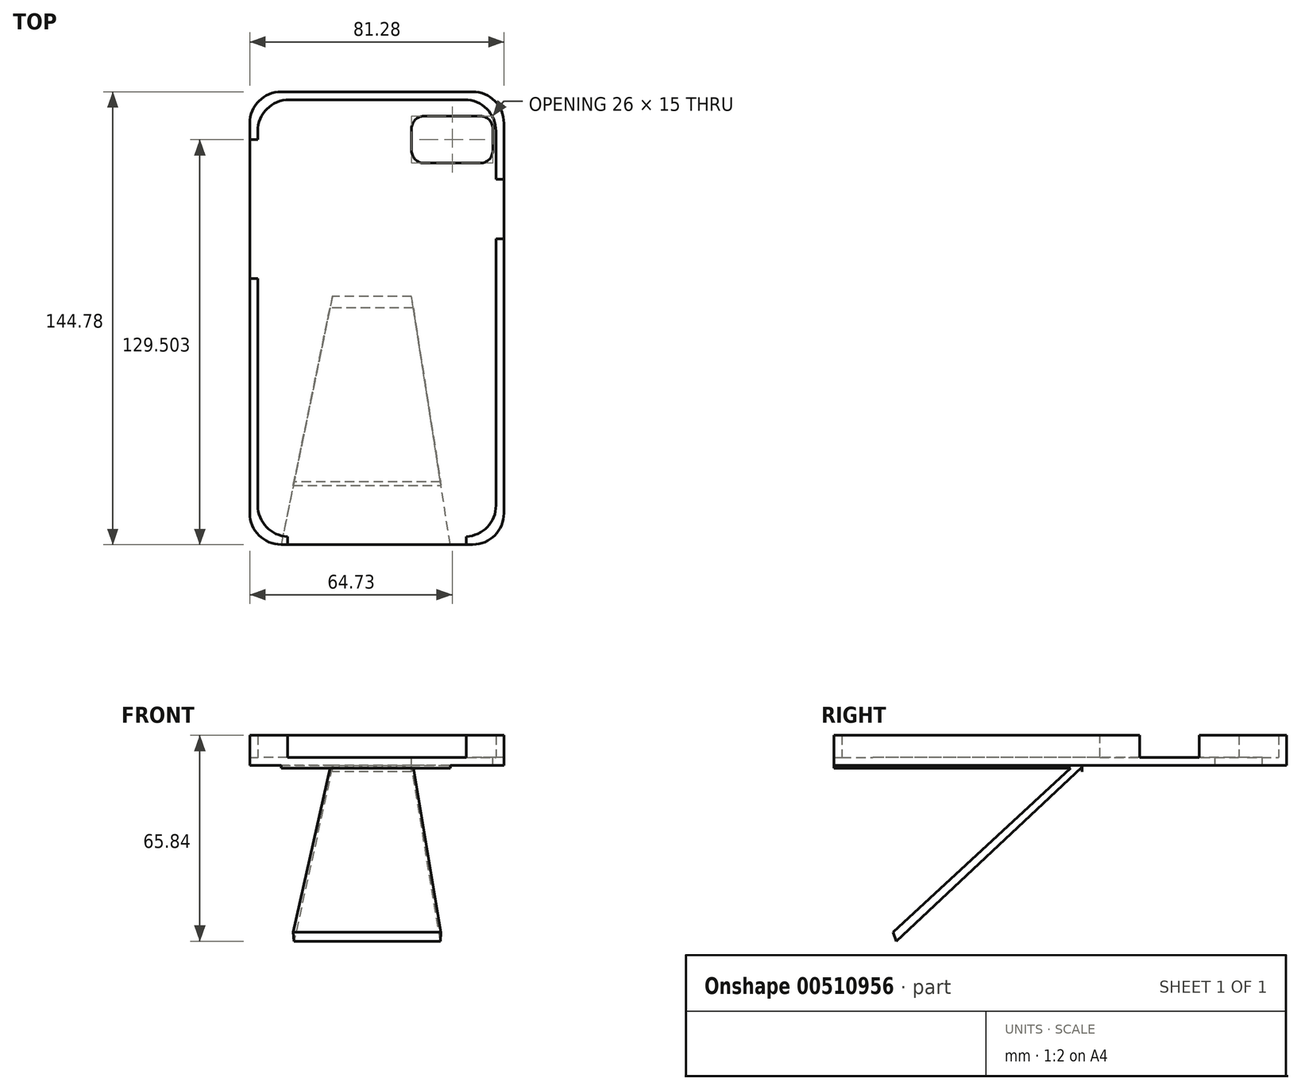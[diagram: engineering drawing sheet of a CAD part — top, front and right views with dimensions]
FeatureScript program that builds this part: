
annotation { "Feature Type Name" : "Feature", "Feature Type Description" : "" }
export const myFeature = defineFeature(function(context is Context, id is Id, definition is map)
    precondition{}
    {
        {
            var Q0;
            Q0=qCreatedBy(makeId("Top.planeOp"),FACE);
            var sketch = newSketch(context, id + "F0", { "sketchPlane" : qUnion([Q0])});
            skLineSegment(sketch, "E0.bottom", {"start": v(-49.2, 70.21) * mm, "end": v(27, 70.21) * mm});
            skLineSegment(sketch, "E0.top", {"start": v(-49.2, -69.49) * mm, "end": v(27, -69.49) * mm});
            skLineSegment(sketch, "E0.left", {"start": v(-49.2, 70.21) * mm, "end": v(-49.2, -69.49) * mm});
            skLineSegment(sketch, "E0.right", {"start": v(27, 70.21) * mm, "end": v(27, -69.49) * mm});
            skSolve(sketch);
        }
        {
            var Q0;
            Q0=makeQuery(id+"F0.imprint","IMPRINT",FACE,{"disambiguationData":[TD([[makeQuery(id+"F0.imprint","IMPRINT",EDGE,{"derivedFrom":sQuery(id+"F0.wireOp",EDGE,"E0.bottom")}),-1.0]])]});
            extrude(context, id + "F1", {"entities" : qUnion([Q0]), "depth" : 7.1 * mm, "offsetDistance" : 25 * mm});
        }
        {
            var Q0;
            Q0=makeQuery(id+"F1.opExtrude","CAP_FACE",FACE,{"disambiguationData":[OSD([sQuery(id+"F0.wireOp",EDGE,"E0.bottom"),sQuery(id+"F0.wireOp",EDGE,"E0.top"),sQuery(id+"F0.wireOp",EDGE,"E0.left"),sQuery(id+"F0.wireOp",EDGE,"E0.right")])],"isStart":false});
            shell(context, id + "F2", {"entities" : qUnion([Q0]), "thickness" : 2.54 * mm, "oppositeDirection" : true});
        }
        {
            var Q0;
            Q0=makeQuery(id+"F2.opShell","OFFSET_FACE",FACE,{"disambiguationData":[OSD([sQuery(id+"F0.wireOp",EDGE,"E0.left")])]});
            var sketch = newSketch(context, id + "F3", { "sketchPlane" : qUnion([Q0])});
            skLineSegment(sketch, "E1.bottom", {"start": v(57.51, 7.1) * mm, "end": v(13.06, 7.1) * mm});
            skLineSegment(sketch, "E1.top", {"start": v(57.51, 0) * mm, "end": v(13.06, 0) * mm});
            skLineSegment(sketch, "E1.left", {"start": v(57.51, 7.1) * mm, "end": v(57.51, 0) * mm});
            skLineSegment(sketch, "E1.right", {"start": v(13.06, 7.1) * mm, "end": v(13.06, 0) * mm});
            skSolve(sketch);
        }
        {
            var Q0;
            Q0=makeQuery(id+"F3.imprint","IMPRINT",FACE,{"disambiguationData":[TD([[makeQuery(id+"F3.imprint","IMPRINT",EDGE,{"derivedFrom":sQuery(id+"F3.wireOp",EDGE,"E1.bottom")}),1.0]])]});
            var Q1;
            Q1=makeQuery(id+"F1.opExtrude","SWEPT_FACE",FACE,{"disambiguationData":[OSD([sQuery(id+"F0.wireOp",EDGE,"E0.left")])]});
            extrude(context, id + "F4", {"entities" : qUnion([Q0, Q1]), "operationType" : NewBodyOperationType.REMOVE, "oppositeDirection" : true, "depth" : 25.4 * mm});
        }
        {
            var Q0;
            Q0=makeQuery(id+"F2.opShell","OFFSET_FACE",FACE,{"disambiguationData":[OSD([sQuery(id+"F0.wireOp",EDGE,"E0.right")])]});
            var sketch = newSketch(context, id + "F5", { "sketchPlane" : qUnion([Q0])});
            skLineSegment(sketch, "E2.bottom", {"start": v(-44.81, 7.1) * mm, "end": v(-25.76, 7.1) * mm});
            skLineSegment(sketch, "E2.top", {"start": v(-44.81, 0) * mm, "end": v(-25.76, 0) * mm});
            skLineSegment(sketch, "E2.left", {"start": v(-44.81, 7.1) * mm, "end": v(-44.81, 0) * mm});
            skLineSegment(sketch, "E2.right", {"start": v(-25.76, 7.1) * mm, "end": v(-25.76, 0) * mm});
            skSolve(sketch);
        }
        {
            var Q0;
            Q0=makeQuery(id+"F5.imprint","IMPRINT",FACE,{"disambiguationData":[TD([[makeQuery(id+"F5.imprint","IMPRINT",EDGE,{"derivedFrom":sQuery(id+"F5.wireOp",EDGE,"E2.bottom")}),-1.0]])]});
            extrude(context, id + "F6", {"entities" : qUnion([Q0]), "operationType" : NewBodyOperationType.REMOVE, "oppositeDirection" : true, "depth" : 25.4 * mm});
        }
        {
            var Q0;
            Q0=makeQuery(id+"F2.opShell","OFFSET_FACE",FACE,{"disambiguationData":[OSD([sQuery(id+"F0.wireOp",EDGE,"E0.top")])]});
            var sketch = newSketch(context, id + "F7", { "sketchPlane" : qUnion([Q0])});
            skLineSegment(sketch, "E3.bottom", {"start": v(-17.48, 7.1) * mm, "end": v(39.67, 7.1) * mm});
            skLineSegment(sketch, "E3.top", {"start": v(-17.48, 0) * mm, "end": v(39.67, 0) * mm});
            skLineSegment(sketch, "E3.left", {"start": v(-17.48, 7.1) * mm, "end": v(-17.48, 0) * mm});
            skLineSegment(sketch, "E3.right", {"start": v(39.67, 7.1) * mm, "end": v(39.67, 0) * mm});
            skSolve(sketch);
        }
        {
            var Q0;
            Q0 = qSketchRegion(id + "F7", true);
            extrude(context, id + "F8", {"entities" : qUnion([Q0]), "operationType" : NewBodyOperationType.REMOVE, "oppositeDirection" : true, "depth" : 25.4 * mm});
        }
        {
            var Q0;
            Q0=makeQuery(id+"F2.opShell","OFFSET_EDGE",EDGE,{"disambiguationData":[OSD([sQuery(id+"F0.wireOp",EDGE,"E0.bottom"),sQuery(id+"F0.wireOp",EDGE,"E0.right")])]});
            var Q1;
            Q1=makeQuery(id+"F2.opShell","OFFSET_EDGE",EDGE,{"disambiguationData":[OSD([sQuery(id+"F0.wireOp",EDGE,"E0.bottom"),sQuery(id+"F0.wireOp",EDGE,"E0.left")])]});
            var Q2;
            Q2=makeQuery(id+"F2.opShell","OFFSET_EDGE",EDGE,{"disambiguationData":[OSD([sQuery(id+"F0.wireOp",EDGE,"E0.top"),sQuery(id+"F0.wireOp",EDGE,"E0.left")])]});
            var Q3;
            Q3=makeQuery(id+"F2.opShell","OFFSET_EDGE",EDGE,{"disambiguationData":[OSD([sQuery(id+"F0.wireOp",EDGE,"E0.top"),sQuery(id+"F0.wireOp",EDGE,"E0.right")])]});
            fillet(context, id + "F9", {"entities" : qUnion([Q0, Q1, Q2, Q3]), "radius" : 10 * mm, "tangentPropagation" : true, "allowEdgeOverflow" : false});
        }
        {
            var Q0;
            Q0=makeQuery(id+"F1.opExtrude","SWEPT_EDGE",EDGE,{"disambiguationData":[OSD([sQuery(id+"F0.wireOp",EDGE,"E0.top"),sQuery(id+"F0.wireOp",EDGE,"E0.right")])]});
            var Q1;
            Q1=makeQuery(id+"F1.opExtrude","SWEPT_EDGE",EDGE,{"disambiguationData":[OSD([sQuery(id+"F0.wireOp",EDGE,"E0.top"),sQuery(id+"F0.wireOp",EDGE,"E0.left")])]});
            var Q2;
            Q2=makeQuery(id+"F1.opExtrude","SWEPT_EDGE",EDGE,{"disambiguationData":[OSD([sQuery(id+"F0.wireOp",EDGE,"E0.bottom"),sQuery(id+"F0.wireOp",EDGE,"E0.right")])]});
            var Q3;
            Q3=makeQuery(id+"F1.opExtrude","SWEPT_EDGE",EDGE,{"disambiguationData":[OSD([sQuery(id+"F0.wireOp",EDGE,"E0.bottom"),sQuery(id+"F0.wireOp",EDGE,"E0.left")])]});
            fillet(context, id + "F10", {"entities" : qUnion([Q0, Q1, Q2, Q3]), "radius" : 10 * mm, "tangentPropagation" : true, "allowEdgeOverflow" : false});
        }
        {
            var Q0;
            Q0=makeQuery(id+"F8.boolean.opBoolean","MERGE",FACE,{"derivedFrom":[makeQuery(id+"F6.boolean.opBoolean","MERGE",FACE,{"derivedFrom":[makeQuery(id+"F4.boolean.opBoolean","MERGE",FACE,{"derivedFrom":[makeQuery(id+"F2.opShell","OFFSET_FACE",FACE,{"disambiguationData":[OSD([sQuery(id+"F0.wireOp",EDGE,"E0.bottom"),sQuery(id+"F0.wireOp",EDGE,"E0.top"),sQuery(id+"F0.wireOp",EDGE,"E0.left"),sQuery(id+"F0.wireOp",EDGE,"E0.right")])]}),makeQuery(id+"F4.opExtrude","SWEPT_FACE",FACE,{"disambiguationData":[OSD([sQuery(id+"F3.wireOp",EDGE,"E1.top")])]})]}),makeQuery(id+"F6.opExtrude","SWEPT_FACE",FACE,{"disambiguationData":[OSD([sQuery(id+"F5.wireOp",EDGE,"E2.top")])]})]}),makeQuery(id+"F8.opExtrude","SWEPT_FACE",FACE,{"disambiguationData":[OSD([sQuery(id+"F7.wireOp",EDGE,"E3.top")])]})]});
            var sketch = newSketch(context, id + "F11", { "sketchPlane" : qUnion([Q0])});
            skLineSegment(sketch, "E4.bottom", {"start": v(4, 64.97) * mm, "end": v(22, 64.97) * mm});
            skLineSegment(sketch, "E4.top", {"start": v(4, 49.97) * mm, "end": v(22, 49.97) * mm});
            skLineSegment(sketch, "E4.left", {"start": v(0, 60.97) * mm, "end": v(0, 53.97) * mm});
            skLineSegment(sketch, "E4.right", {"start": v(26, 60.97) * mm, "end": v(26, 53.97) * mm});
            skPoint(sketch, "E5.visualSharp", {"position": v(0, 49.97) * mm});
            skArc(sketch, "E5.filletArc", {"start": v(0, 53.97) * mm, "mid": v(1.17, 51.14) * mm, "end": v(4, 49.97) * mm});
            skPoint(sketch, "E6.visualSharp", {"position": v(0, 64.97) * mm});
            skArc(sketch, "E6.filletArc", {"start": v(4, 64.97) * mm, "mid": v(1.17, 63.8) * mm, "end": v(0, 60.97) * mm});
            skPoint(sketch, "E7.visualSharp", {"position": v(26, 64.97) * mm});
            skArc(sketch, "E7.filletArc", {"start": v(26, 60.97) * mm, "mid": v(24.83, 63.8) * mm, "end": v(22, 64.97) * mm});
            skPoint(sketch, "E8.visualSharp", {"position": v(26, 49.97) * mm});
            skArc(sketch, "E8.filletArc", {"start": v(22, 49.97) * mm, "mid": v(24.83, 51.14) * mm, "end": v(26, 53.97) * mm});
            skSolve(sketch);
        }
        {
            var Q0;
            Q0=makeQuery(id+"F11.imprint","IMPRINT",FACE,{"disambiguationData":[TD([[makeQuery(id+"F11.imprint","IMPRINT",EDGE,{"derivedFrom":sQuery(id+"F11.wireOp",EDGE,"E4.bottom")}),-1.0]])]});
            extrude(context, id + "F12", {"entities" : qUnion([Q0]), "operationType" : NewBodyOperationType.REMOVE, "oppositeDirection" : true, "depth" : 25 * mm, "offsetDistance" : 25 * mm});
        }
        {
            var Q0;
            Q0=makeQuery(id+"F1.opExtrude","CAP_FACE",FACE,{"disambiguationData":[OSD([sQuery(id+"F0.wireOp",EDGE,"E0.bottom"),sQuery(id+"F0.wireOp",EDGE,"E0.top"),sQuery(id+"F0.wireOp",EDGE,"E0.left"),sQuery(id+"F0.wireOp",EDGE,"E0.right")])],"isStart":true});
            var sketch = newSketch(context, id + "F13", { "sketchPlane" : qUnion([Q0])});
            skLineSegment(sketch, "E9", {"start": v(0, -7.34) * mm, "end": v(-25.34, -7.34) * mm});
            skLineSegment(sketch, "E10", {"start": v(-25.34, -7.34) * mm, "end": v(-41.73, 72.03) * mm});
            skLineSegment(sketch, "E11", {"start": v(-41.73, 72.03) * mm, "end": v(12.38, 72.03) * mm});
            skLineSegment(sketch, "E12", {"start": v(12.38, 72.03) * mm, "end": v(0, -7.34) * mm});
            skSolve(sketch);
        }
        {
            var Q0;
            Q0=makeQuery(id+"F1.opExtrude","SWEPT_FACE",FACE,{"disambiguationData":[OSD([sQuery(id+"F0.wireOp",EDGE,"E0.left")])]});
            var sketch = newSketch(context, id + "F14", { "sketchPlane" : qUnion([Q0])});
            skSolve(sketch);
        }
        {
            var Q0;
            Q0 = qSketchRegion(id + "F14", true);
            var Q1;
            Q1=makeQuery(id+"F13.imprint","IMPRINT",FACE,{"disambiguationData":[TD([[makeQuery(id+"F13.imprint","IMPRINT",EDGE,{"derivedFrom":sQuery(id+"F13.wireOp",EDGE,"E9")}),-1.0]])]});
            extrude(context, id + "F15", {"entities" : qUnion([Q0, Q1]), "operationType" : NewBodyOperationType.ADD, "depth" : 75 * mm, "offsetDistance" : 25 * mm});
        }
        {
            var Q0;
            {var subQ0=sQuery(id+"F0.wireOp",EDGE,"E0.left");Q0=makeQuery(id+"F14.imprint","IMPRINT",FACE,{"disambiguationData":[TD([[makeQuery(id+"F14.imprint","IMPRINT",EDGE,{"derivedFrom":makeQuery(id+"F1.opExtrude","CAP_EDGE",EDGE,{"disambiguationData":[OSD([subQ0])],"isStart":true})}),1.0]])]});}
            var sketch = newSketch(context, id + "F16", { "sketchPlane" : qUnion([Q0])});
            skLineSegment(sketch, "E13", {"start": v(-7.27, -3.12) * mm, "end": v(75.58, -80.86) * mm});
            skLineSegment(sketch, "E14", {"start": v(75.58, -80.86) * mm, "end": v(-11.17, -80.86) * mm});
            skLineSegment(sketch, "E15", {"start": v(-11.17, -80.86) * mm, "end": v(-7.27, -3.12) * mm});
            skSolve(sketch);
        }
        {
            var Q0;
            Q0 = qSketchRegion(id + "F16", true);
            extrude(context, id + "F17", {"entities" : qUnion([Q0]), "operationType" : NewBodyOperationType.REMOVE, "oppositeDirection" : true, "depth" : 111.1 * mm, "offsetDistance" : 25 * mm});
        }
        {
            var Q0;
            {var subQ0=sQuery(id+"F0.wireOp",EDGE,"E0.left");Q0=makeQuery(id+"F14.imprint","IMPRINT",FACE,{"disambiguationData":[TD([[makeQuery(id+"F14.imprint","IMPRINT",EDGE,{"derivedFrom":makeQuery(id+"F1.opExtrude","CAP_EDGE",EDGE,{"disambiguationData":[OSD([subQ0])],"isStart":true})}),1.0]])]});}
            var sketch = newSketch(context, id + "F18", { "sketchPlane" : qUnion([Q0])});
            skLineSegment(sketch, "E16", {"start": v(-3.66, -3.42) * mm, "end": v(72.28, -3.42) * mm});
            skLineSegment(sketch, "E17", {"start": v(72.28, -3.42) * mm, "end": v(55.17, -57.75) * mm});
            skLineSegment(sketch, "E18", {"start": v(55.17, -57.75) * mm, "end": v(-3.66, -3.42) * mm});
            skSolve(sketch);
        }
        {
            var Q0;
            Q0=makeQuery(id+"F18.imprint","IMPRINT",FACE,{"disambiguationData":[TD([[makeQuery(id+"F18.imprint","IMPRINT",EDGE,{"derivedFrom":sQuery(id+"F18.wireOp",EDGE,"E16")}),-1.0]])]});
            extrude(context, id + "F19", {"entities" : qUnion([Q0]), "operationType" : NewBodyOperationType.REMOVE, "oppositeDirection" : true, "depth" : 75.7 * mm, "offsetDistance" : 25 * mm});
        }
        {
            var Q0;
            {var subQ0=sQuery(id+"F0.wireOp",EDGE,"E0.left");Q0=makeQuery(id+"F14.imprint","IMPRINT",FACE,{"disambiguationData":[TD([[makeQuery(id+"F14.imprint","IMPRINT",EDGE,{"derivedFrom":makeQuery(id+"F1.opExtrude","CAP_EDGE",EDGE,{"disambiguationData":[OSD([subQ0])],"isStart":true})}),1.0]])]});}
            var sketch = newSketch(context, id + "F20", { "sketchPlane" : qUnion([Q0])});
            skLineSegment(sketch, "E19", {"start": v(72.28, -3.12) * mm, "end": v(72.28, -83.57) * mm});
            skLineSegment(sketch, "E20", {"start": v(72.28, -83.57) * mm, "end": v(50.06, -64.06) * mm});
            skLineSegment(sketch, "E21", {"start": v(50.06, -64.06) * mm, "end": v(72.28, -3.12) * mm});
            skSolve(sketch);
        }
        {
            var Q0;
            Q0 = qSketchRegion(id + "F20", true);
            extrude(context, id + "F21", {"entities" : qUnion([Q0]), "operationType" : NewBodyOperationType.REMOVE, "oppositeDirection" : true, "depth" : 83.5 * mm, "offsetDistance" : 25 * mm});
        }
    });
